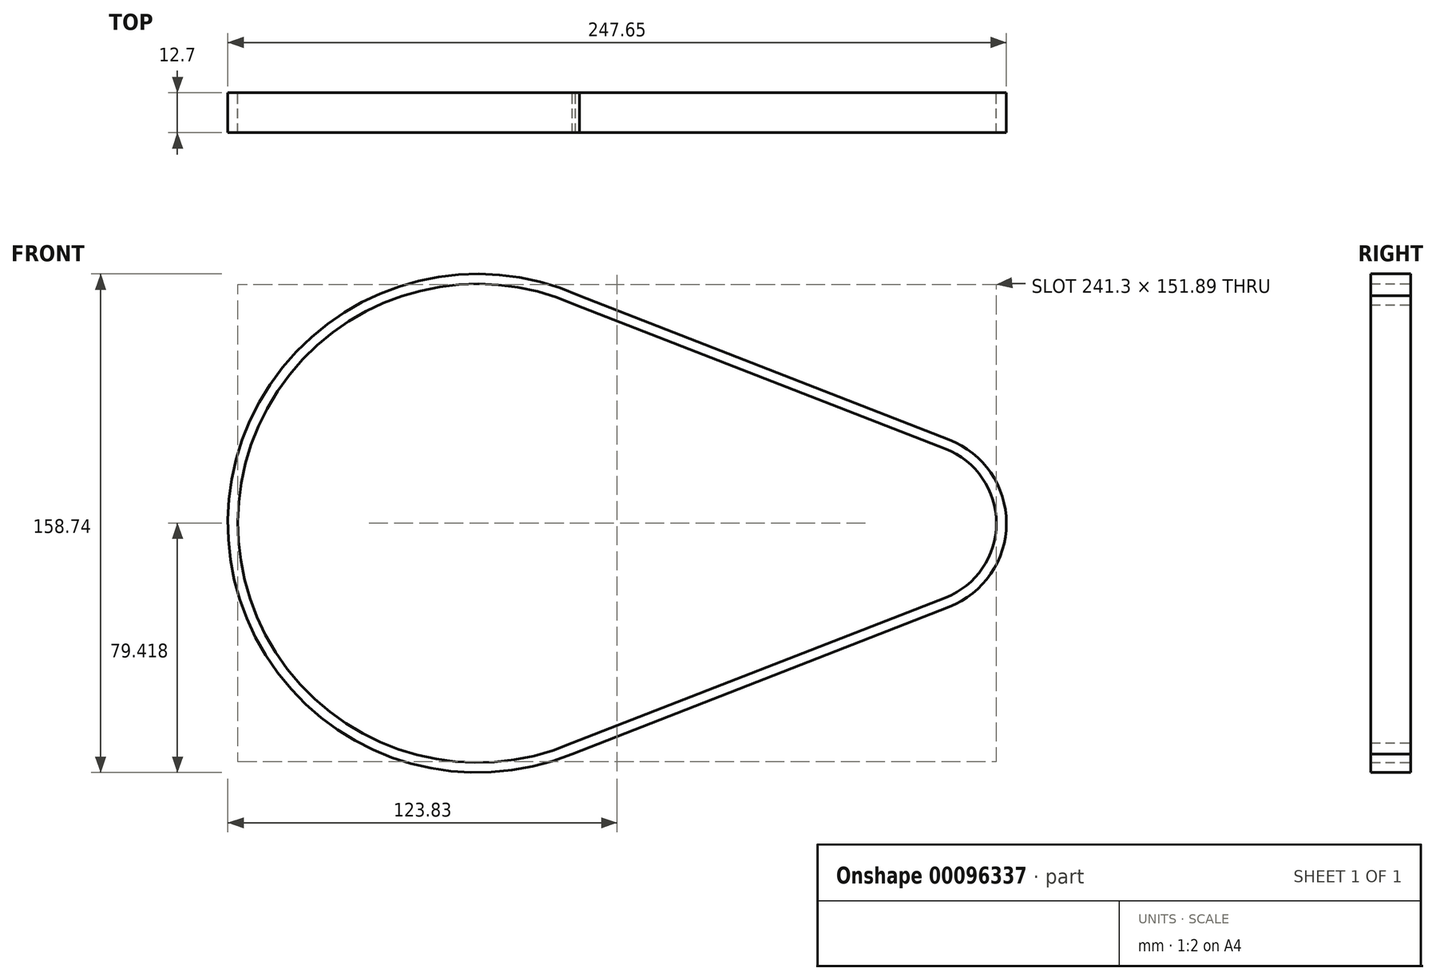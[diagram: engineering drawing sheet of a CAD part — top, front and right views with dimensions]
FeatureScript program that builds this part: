
annotation { "Feature Type Name" : "Feature", "Feature Type Description" : "" }
export const myFeature = defineFeature(function(context is Context, id is Id, definition is map)
    precondition{}
    {
        {
            var Q0;
            Q0=qCreatedBy(makeId("Front.planeOp"),FACE);
            var sketch = newSketch(context, id + "F0", { "sketchPlane" : qUnion([Q0])});
            skArc(sketch, "E0", {"start": v(-36.06, 69.5) * mm, "mid": v(-143.49, 0.58) * mm, "end": v(-37.13, -69.97) * mm});
            skArc(sketch, "E1", {"start": v(81.64, -23.66) * mm, "mid": v(97.8, 0) * mm, "end": v(81.63, 23.67) * mm});
            skArc(sketch, "E2", {"start": v(-34.83, 72.43) * mm, "mid": v(-146.66, 1.25) * mm, "end": v(-37.13, -73.42) * mm});
            skArc(sketch, "E3", {"start": v(82.8, -26.62) * mm, "mid": v(100.98, 0) * mm, "end": v(82.78, 26.63) * mm});
            skLineSegment(sketch, "E4", {"start": v(-42.21, 75.3) * mm, "end": v(82.78, 26.63) * mm});
            skLineSegment(sketch, "E5", {"start": v(-37.13, -73.42) * mm, "end": v(82.8, -26.62) * mm});
            skLineSegment(sketch, "E6", {"start": v(-43.29, 72.32) * mm, "end": v(81.63, 23.67) * mm});
            skLineSegment(sketch, "E7", {"start": v(-37.13, -69.97) * mm, "end": v(81.64, -23.66) * mm});
            skSolve(sketch);
        }
        {
            var Q0;
            Q0 = qSketchRegion(id + "F0", true);
            extrude(context, id + "F1", {"entities" : qUnion([Q0]), "depth" : 12.7 * mm});
        }
    });
